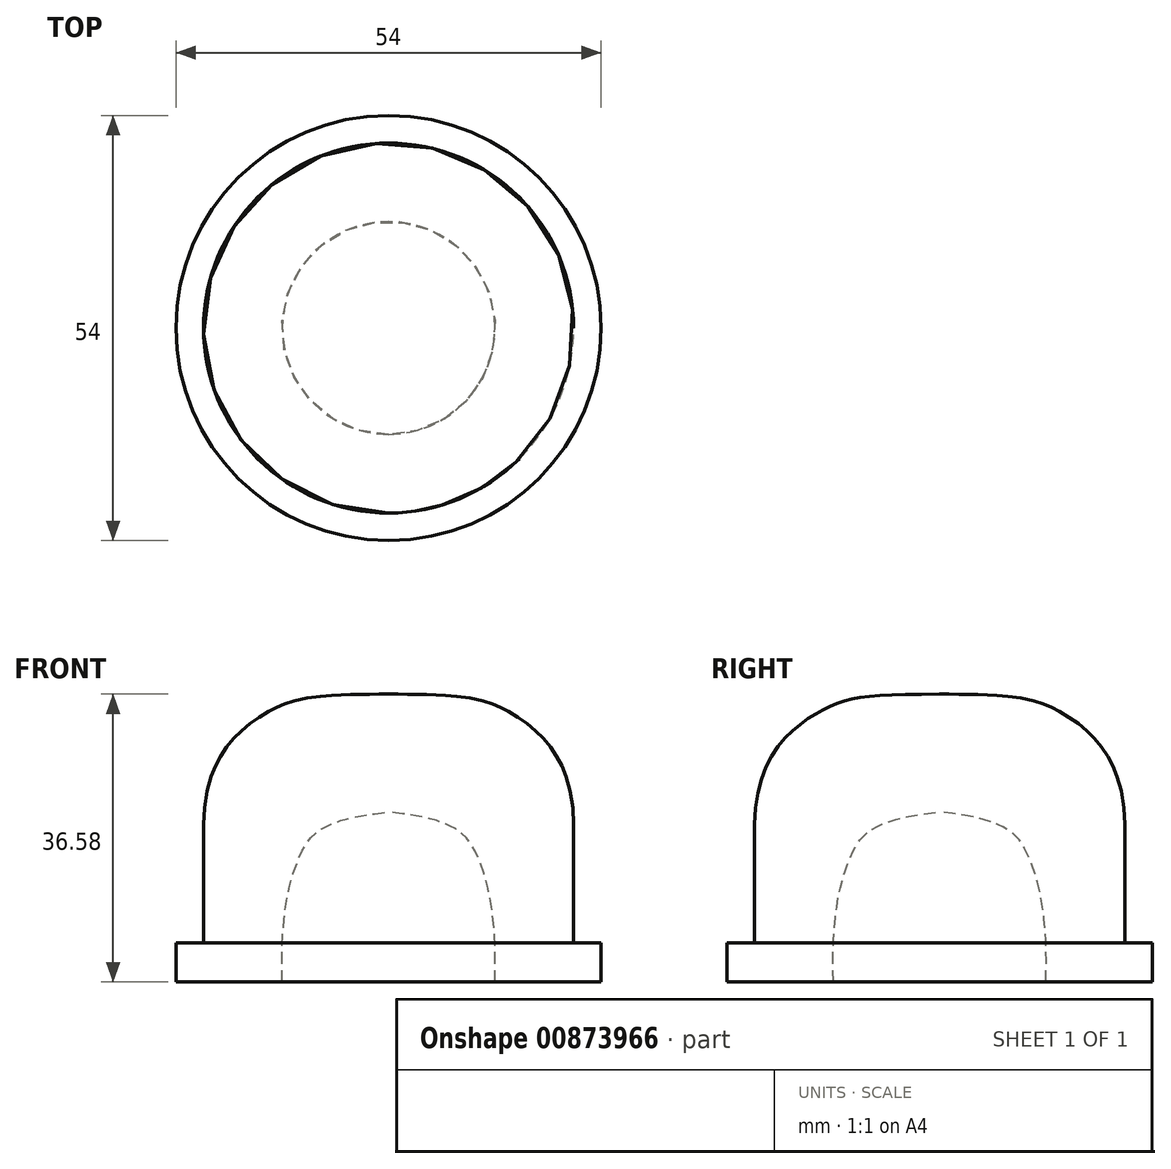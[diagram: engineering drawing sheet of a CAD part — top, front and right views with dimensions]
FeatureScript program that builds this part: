
annotation { "Feature Type Name" : "Feature", "Feature Type Description" : "" }
export const myFeature = defineFeature(function(context is Context, id is Id, definition is map)
    precondition{}
    {
        {
            var Q0;
            Q0=qCreatedBy(makeId("Right.planeOp"),FACE);
            var sketch = newSketch(context, id + "F0", { "sketchPlane" : qUnion([Q0])});
            skLineSegment(sketch, "E0", {"start": v(0, 0) * mm, "end": v(-27, 0) * mm});
            skLineSegment(sketch, "E1", {"start": v(-27, 0) * mm, "end": v(-27, 5) * mm});
            skLineSegment(sketch, "E2", {"start": v(-27, 5) * mm, "end": v(-23.5, 5) * mm});
            skLineSegment(sketch, "E3", {"start": v(-23.5, 5) * mm, "end": v(-23.5, 45) * mm});
            skLineSegment(sketch, "E4", {"start": v(-23.5, 45) * mm, "end": v(0, 45) * mm});
            skLineSegment(sketch, "E5", {"start": v(0, 45) * mm, "end": v(0, 0) * mm});
            skFitSpline(sketch, "E6", {"points": [v(-13.5, 0) * mm, v(-11.3, 15.96) * mm, v(0, 21.58) * mm], "startDerivative": vector(-1.53, 44.56) * mm, "endDerivative": vector(53.13, 5.04) * mm});
            skFitSpline(sketch, "E7", {"points": [v(0, 36.58) * mm, v(-14.98, 34.48) * mm, v(-23.5, 20) * mm], "startDerivative": vector(-56.69, -0.51) * mm, "endDerivative": vector(0, -51.17) * mm});
            skSolve(sketch);
        }
        {
            var Q0;
            {var subQ0=sQuery(id+"F0.wireOp",EDGE,"E1");Q0=makeQuery(id+"F0.imprint","IMPRINT",FACE,{"disambiguationData":[TD([[makeQuery(id+"F0.imprint","IMPRINT",EDGE,{"derivedFrom":subQ0}),-1.0]])]});}
            var Q1;
            Q1=sQuery(id+"F0.wireOp",EDGE,"E5");
            revolve(context, id + "F1", {"surfaceOperationType" : NewSurfaceOperationType.NEW, "entities" : qUnion([Q0]), "axis" : qUnion([Q1]), "revolveType" : RevolveType.FULL});
        }
    });
